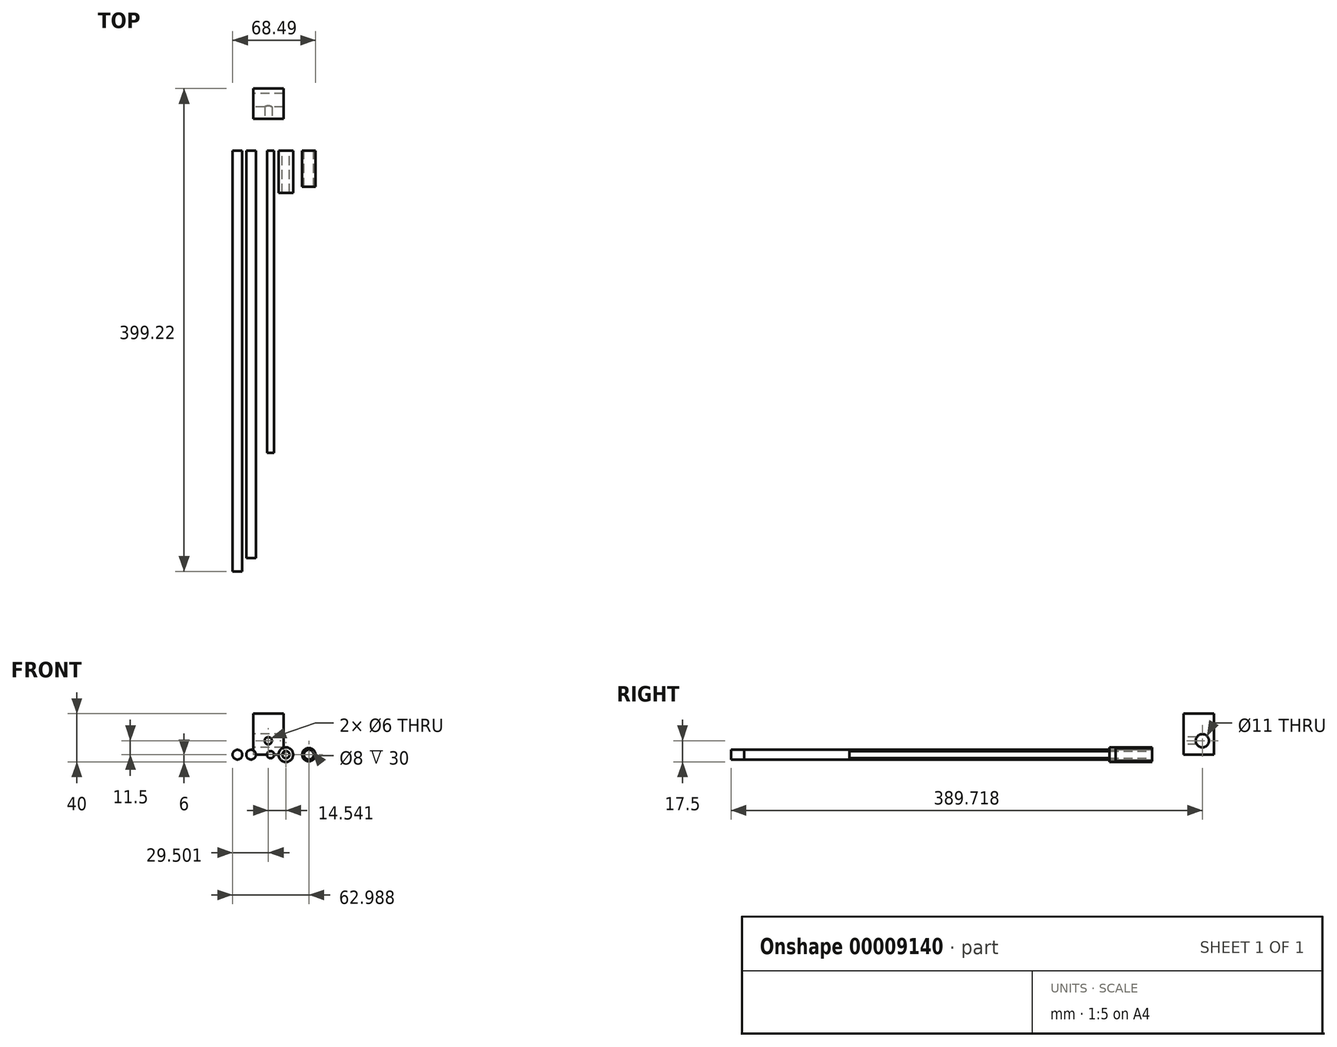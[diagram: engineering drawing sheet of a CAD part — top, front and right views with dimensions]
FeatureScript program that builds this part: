
annotation { "Feature Type Name" : "Feature", "Feature Type Description" : "" }
export const myFeature = defineFeature(function(context is Context, id is Id, definition is map)
    precondition{}
    {
        {
            var Q0;
            Q0=qCreatedBy(makeId("Front.planeOp"),FACE);
            var sketch = newSketch(context, id + "F0", { "sketchPlane" : qUnion([Q0])});
            skCircle(sketch, "E0", {"center": v(-61.9, 0) * mm, "radius": 4 * mm});
            skSolve(sketch);
        }
        {
            var Q0;
            Q0=makeQuery(id+"F0.imprint","IMPRINT",FACE,{"disambiguationData":[TD([[makeQuery(id+"F0.imprint","IMPRINT",EDGE,{"derivedFrom":sQuery(id+"F0.wireOp",EDGE,"E0")}),1.0]])]});
            extrude(context, id + "F1", {"entities" : qUnion([Q0]), "depth" : 348 * mm});
        }
        {
            var Q0;
            Q0=qCreatedBy(makeId("Front.planeOp"),FACE);
            var sketch = newSketch(context, id + "F2", { "sketchPlane" : qUnion([Q0])});
            skCircle(sketch, "E1", {"center": v(-45.77, 0) * mm, "radius": 3 * mm});
            skSolve(sketch);
        }
        {
            var Q0;
            Q0=makeQuery(id+"F2.imprint","IMPRINT",FACE,{"disambiguationData":[TD([[makeQuery(id+"F2.imprint","IMPRINT",EDGE,{"derivedFrom":sQuery(id+"F2.wireOp",EDGE,"E1")}),1.0]])]});
            extrude(context, id + "F3", {"entities" : qUnion([Q0]), "depth" : 250 * mm});
        }
        {
            var Q0;
            Q0=qCreatedBy(makeId("Front.planeOp"),FACE);
            var sketch = newSketch(context, id + "F4", { "sketchPlane" : qUnion([Q0])});
            skCircle(sketch, "E2", {"center": v(-33.08, 0) * mm, "radius": 3 * mm});
            skCircle(sketch, "E3", {"center": v(-33.08, 0) * mm, "radius": 6 * mm});
            skSolve(sketch);
        }
        {
            var Q0;
            Q0=makeQuery(id+"F4.imprint","IMPRINT",FACE,{"disambiguationData":[TD([[makeQuery(id+"F4.imprint","IMPRINT",EDGE,{"derivedFrom":sQuery(id+"F4.wireOp",EDGE,"E2")}),-1.0]])]});
            extrude(context, id + "F5", {"entities" : qUnion([Q0]), "depth" : 35 * mm});
        }
        {
            var Q0;
            Q0=makeQuery(id+"F1.opExtrude","SWEPT_BODY",BODY,{"disambiguationData":[OSD([sQuery(id+"F0.wireOp",EDGE,"E0")])]});
            transform(context, id + "F6", {"entities" : qUnion([Q0]), "transformType" : TransformType.TRANSLATION_3D, "dx" : -11.23 * mm, "dy" : 0 * mm, "dz" : 0 * mm, "makeCopy" : false});
        }
        {
            var Q0;
            Q0 = qSketchRegion(id + "F0", true);
            extrude(context, id + "F7", {"entities" : qUnion([Q0]), "depth" : 337 * mm});
        }
        {
            var Q0;
            Q0=qCreatedBy(makeId("Front.planeOp"),FACE);
            var sketch = newSketch(context, id + "F8", { "sketchPlane" : qUnion([Q0])});
            skCircle(sketch, "E4", {"center": v(-14.13, 0) * mm, "radius": 4 * mm});
            skCircle(sketch, "E5", {"center": v(-14.13, 0) * mm, "radius": 5.5 * mm});
            skSolve(sketch);
        }
        {
            var Q0;
            Q0=makeQuery(id+"F8.imprint","IMPRINT",FACE,{"disambiguationData":[TD([[makeQuery(id+"F8.imprint","IMPRINT",EDGE,{"derivedFrom":sQuery(id+"F8.wireOp",EDGE,"E4")}),-1.0]])]});
            extrude(context, id + "F9", {"entities" : qUnion([Q0]), "depth" : 30 * mm});
        }
        {
            var Q0;
            Q0=qCreatedBy(makeId("Top.planeOp"),FACE);
            var sketch = newSketch(context, id + "F10", { "sketchPlane" : qUnion([Q0])});
            skLineSegment(sketch, "E6.bottom", {"start": v(-35.12, 51.22) * mm, "end": v(-60.12, 51.22) * mm});
            skLineSegment(sketch, "E6.top", {"start": v(-35.12, 26.22) * mm, "end": v(-60.12, 26.22) * mm});
            skLineSegment(sketch, "E6.left", {"start": v(-35.12, 51.22) * mm, "end": v(-35.12, 26.22) * mm});
            skLineSegment(sketch, "E6.right", {"start": v(-60.12, 51.22) * mm, "end": v(-60.12, 26.22) * mm});
            skSolve(sketch);
        }
        {
            var Q0;
            Q0=makeQuery(id+"F10.imprint","IMPRINT",FACE,{"disambiguationData":[TD([[makeQuery(id+"F10.imprint","IMPRINT",EDGE,{"derivedFrom":sQuery(id+"F10.wireOp",EDGE,"E6.bottom")}),1.0]])]});
            extrude(context, id + "F11", {"entities" : qUnion([Q0]), "depth" : 34 * mm});
        }
        {
            var Q0;
            Q0=makeQuery(id+"F11.opExtrude","SWEPT_FACE",FACE,{"disambiguationData":[OSD([sQuery(id+"F10.wireOp",EDGE,"E6.right")])]});
            var sketch = newSketch(context, id + "F12", { "sketchPlane" : qUnion([Q0])});
            skLineSegment(sketch, "E7", {"start": v(-32.12, 0) * mm, "end": v(-51.22, 0) * mm, "construction": true});
            skLineSegment(sketch, "E8", {"start": v(-51.22, 0) * mm, "end": v(-51.22, 22.36) * mm, "construction": true});
            skCircle(sketch, "E9", {"center": v(-41.72, 11.5) * mm, "radius": 5.5 * mm});
            skSolve(sketch);
        }
        {
            var Q0;
            Q0=makeQuery(id+"F12.imprint","IMPRINT",FACE,{"disambiguationData":[TD([[makeQuery(id+"F12.imprint","IMPRINT",EDGE,{"derivedFrom":sQuery(id+"F12.wireOp",EDGE,"E9")}),1.0]])]});
            extrude(context, id + "F13", {"entities" : qUnion([Q0]), "operationType" : NewBodyOperationType.REMOVE, "endBound" : BoundingType.THROUGH_ALL, "oppositeDirection" : true, "depth" : 25 * mm});
        }
        {
            var Q0;
            Q0=makeQuery(id+"F11.opExtrude","SWEPT_FACE",FACE,{"disambiguationData":[OSD([sQuery(id+"F10.wireOp",EDGE,"E6.top")])]});
            var sketch = newSketch(context, id + "F14", { "sketchPlane" : qUnion([Q0])});
            skLineSegment(sketch, "E10.0", {"start": v(-60.12, 6) * mm, "end": v(-60.12, 17) * mm, "construction": true});
            skLineSegment(sketch, "E11", {"start": v(-60.12, 17) * mm, "end": v(-35.12, 17) * mm, "construction": true});
            skLineSegment(sketch, "E12", {"start": v(-60.12, 6) * mm, "end": v(-35.12, 6) * mm, "construction": true});
            skLineSegment(sketch, "E13", {"start": v(-60.12, 17) * mm, "end": v(-60.12, 11.5) * mm, "construction": true});
            skLineSegment(sketch, "E14", {"start": v(-60.12, 11.5) * mm, "end": v(-35.12, 11.5) * mm, "construction": true});
            skCircle(sketch, "E15", {"center": v(-47.62, 11.5) * mm, "radius": 3 * mm});
            skSolve(sketch);
        }
        {
            var Q0;
            Q0=makeQuery(id+"F14.imprint","IMPRINT",FACE,{"disambiguationData":[TD([[makeQuery(id+"F14.imprint","IMPRINT",EDGE,{"derivedFrom":sQuery(id+"F14.wireOp",EDGE,"E15")}),1.0]])]});
            extrude(context, id + "F15", {"entities" : qUnion([Q0]), "operationType" : NewBodyOperationType.REMOVE, "endBound" : BoundingType.UP_TO_NEXT, "oppositeDirection" : true, "depth" : 25 * mm});
        }
    });
